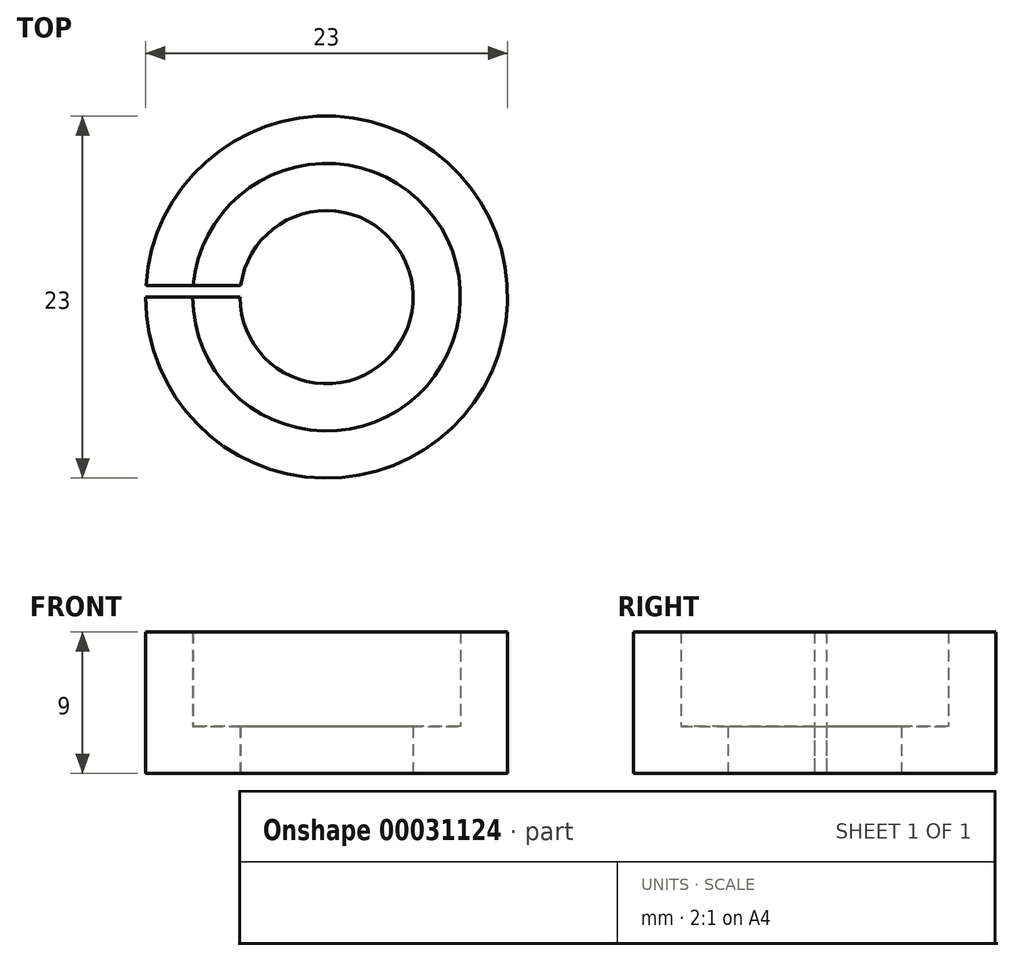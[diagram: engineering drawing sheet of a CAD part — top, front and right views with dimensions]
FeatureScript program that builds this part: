
annotation { "Feature Type Name" : "Feature", "Feature Type Description" : "" }
export const myFeature = defineFeature(function(context is Context, id is Id, definition is map)
    precondition{}
    {
        {
            var Q0;
            Q0=qCreatedBy(makeId("Top.planeOp"),FACE);
            var sketch = newSketch(context, id + "F0", { "sketchPlane" : qUnion([Q0])});
            skCircle(sketch, "E0", {"center": v(0, 0) * mm, "radius": 8.5 * mm});
            skCircle(sketch, "E1.0", {"center": v(0, 0) * mm, "radius": 11.5 * mm});
            skCircle(sketch, "E2.0", {"center": v(0, 0) * mm, "radius": 5.5 * mm});
            skLineSegment(sketch, "E3.bottom", {"start": v(0, 0) * mm, "end": v(-14.82, 0) * mm});
            skLineSegment(sketch, "E3.top", {"start": v(0, 0.75) * mm, "end": v(-14.82, 0.75) * mm});
            skLineSegment(sketch, "E3.left", {"start": v(0, 0) * mm, "end": v(0, 0.75) * mm});
            skLineSegment(sketch, "E3.right", {"start": v(-14.82, 0) * mm, "end": v(-14.82, 0.75) * mm});
            skSolve(sketch);
        }
        {
            var Q0;
            Q0=makeQuery(id+"F0.imprint","IMPRINT",FACE,{"disambiguationData":[TD([[makeQuery(id+"F0.imprint","IMPRINT",EDGE,{"derivedFrom":sQuery(id+"F0.wireOp",EDGE,"E0")}),1.0]])]});
            var Q1;
            Q1=makeQuery(id+"F0.imprint","IMPRINT",FACE,{"disambiguationData":[TD([[makeQuery(id+"F0.imprint","IMPRINT",EDGE,{"derivedFrom":sQuery(id+"F0.wireOp",EDGE,"E0")}),-1.0]])]});
            extrude(context, id + "F1", {"entities" : qUnion([Q0, Q1]), "depth" : 3 * mm});
        }
        {
            var Q0;
            Q0=makeQuery(id+"F0.imprint","IMPRINT",FACE,{"disambiguationData":[TD([[makeQuery(id+"F0.imprint","IMPRINT",EDGE,{"derivedFrom":sQuery(id+"F0.wireOp",EDGE,"E0")}),-1.0]])]});
            extrude(context, id + "F2", {"entities" : qUnion([Q0]), "operationType" : NewBodyOperationType.ADD, "depth" : 9 * mm});
        }
        {
            var Q0;
            {var subQ3=sQuery(id+"F0.wireOp",EDGE,"E0");var subQ5=sQuery(id+"F0.wireOp",EDGE,"E3.bottom");var subQ7=makeQuery(id+"F0.imprint","INTERSECT",VERTEX,{"derivedFrom":[subQ3,subQ5]});Q0=makeQuery(id+"F0.imprint","IMPRINT",FACE,{"disambiguationData":[TD([[makeQuery(id+"F0.imprint","IMPRINT",EDGE,{"disambiguationData":[TD([[subQ7,1.0]])],"derivedFrom":subQ3}),1.0]])]});}
            var Q1;
            {var subQ1=sQuery(id+"F0.wireOp",EDGE,"E0");var subQ5=sQuery(id+"F0.wireOp",EDGE,"E3.bottom");var subQ6=makeQuery(id+"F0.imprint","INTERSECT",VERTEX,{"derivedFrom":[subQ1,subQ5]});Q1=makeQuery(id+"F0.imprint","IMPRINT",FACE,{"disambiguationData":[TD([[makeQuery(id+"F0.imprint","IMPRINT",EDGE,{"disambiguationData":[TD([[subQ6,1.0]])],"derivedFrom":subQ1}),-1.0]])]});}
            extrude(context, id + "F3", {"entities" : qUnion([Q0, Q1]), "operationType" : NewBodyOperationType.REMOVE, "endBound" : BoundingType.THROUGH_ALL, "depth" : 25 * mm});
        }
    });
